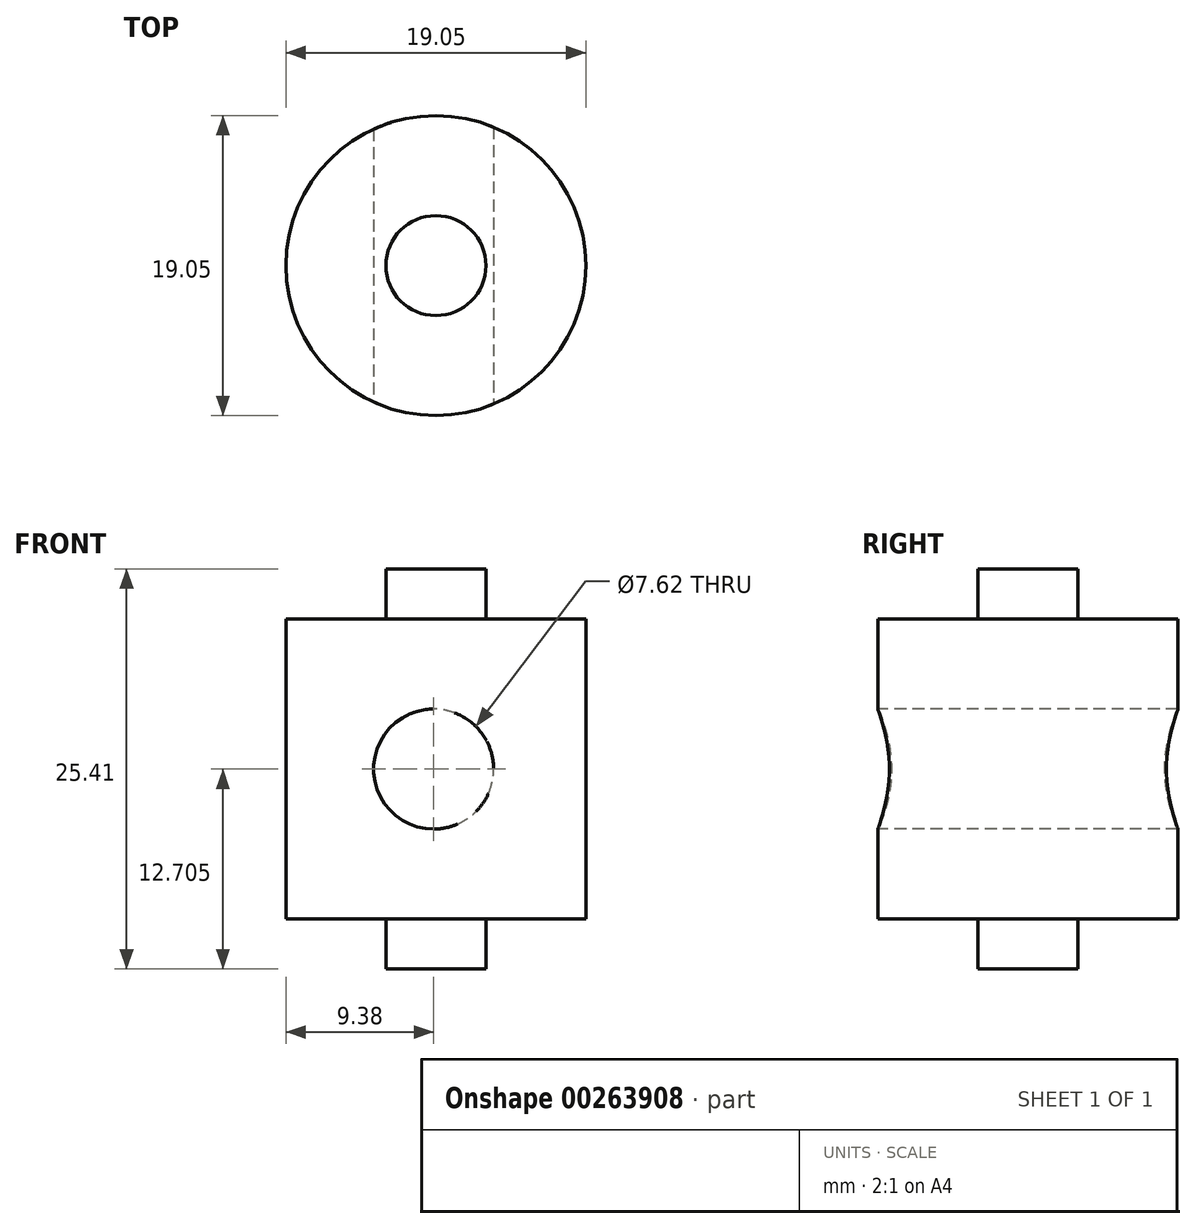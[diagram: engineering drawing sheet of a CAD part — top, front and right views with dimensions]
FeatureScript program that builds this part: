
annotation { "Feature Type Name" : "Feature", "Feature Type Description" : "" }
export const myFeature = defineFeature(function(context is Context, id is Id, definition is map)
    precondition{}
    {
        {
            var Q0;
            Q0=qCreatedBy(makeId("Top.planeOp"),FACE);
            var sketch = newSketch(context, id + "F0", { "sketchPlane" : qUnion([Q0])});
            skCircle(sketch, "E0", {"center": v(0.14, -0.06) * mm, "radius": 9.53 * mm});
            skSolve(sketch);
        }
        {
            var Q0;
            Q0 = qSketchRegion(id + "F0", true);
            extrude(context, id + "F1", {"entities" : qUnion([Q0]), "depth" : 19.05 * mm});
        }
        {
            var Q0;
            Q0=makeQuery(id+"F1.opExtrude","CAP_FACE",FACE,{"disambiguationData":[OSD([sQuery(id+"F0.wireOp",EDGE,"E0")])],"isStart":false});
            var sketch = newSketch(context, id + "F2", { "sketchPlane" : qUnion([Q0])});
            skCircle(sketch, "E1", {"center": v(0.14, -0.06) * mm, "radius": 3.18 * mm});
            skSolve(sketch);
        }
        {
            var Q0;
            Q0 = qSketchRegion(id + "F2", true);
            extrude(context, id + "F3", {"entities" : qUnion([Q0]), "operationType" : NewBodyOperationType.ADD, "depth" : 3.17 * mm});
        }
        {
            var Q0;
            Q0=makeQuery(id+"F1.opExtrude","CAP_FACE",FACE,{"disambiguationData":[OSD([sQuery(id+"F0.wireOp",EDGE,"E0")])],"isStart":true});
            var sketch = newSketch(context, id + "F4", { "sketchPlane" : qUnion([Q0])});
            skCircle(sketch, "E2", {"center": v(0.14, 0.06) * mm, "radius": 3.18 * mm});
            skSolve(sketch);
        }
        {
            var Q0;
            Q0 = qSketchRegion(id + "F4", true);
            extrude(context, id + "F5", {"entities" : qUnion([Q0]), "operationType" : NewBodyOperationType.ADD, "depth" : 3.17 * mm});
        }
        {
            var Q0;
            Q0=qCreatedBy(makeId("Front.planeOp"),FACE);
            var sketch = newSketch(context, id + "F6", { "sketchPlane" : qUnion([Q0])});
            skCircle(sketch, "E3", {"center": v(0, 9.53) * mm, "radius": 3.81 * mm});
            skSolve(sketch);
        }
        {
            var Q0;
            Q0 = qSketchRegion(id + "F6", true);
            extrude(context, id + "F7", {"entities" : qUnion([Q0]), "operationType" : NewBodyOperationType.REMOVE, "oppositeDirection" : true, "depth" : 25.4 * mm});
        }
        {
            var Q0;
            Q0=makeQuery(id+"F7.boolean.opBoolean","COPY",FACE,{"derivedFrom":makeQuery(id+"F7.opExtrude","CAP_FACE",FACE,{"disambiguationData":[OSD([sQuery(id+"F6.wireOp",EDGE,"E3")])],"isStart":true})});
            var sketch = newSketch(context, id + "F8", { "sketchPlane" : qUnion([Q0])});
            skCircle(sketch, "E4", {"center": v(0, 9.53) * mm, "radius": 3.81 * mm});
            skSolve(sketch);
        }
        {
            var Q0;
            Q0 = qSketchRegion(id + "F8", true);
            extrude(context, id + "F9", {"entities" : qUnion([Q0]), "operationType" : NewBodyOperationType.REMOVE, "oppositeDirection" : true, "depth" : 25.4 * mm});
        }
    });
